# Revit family: IS_Idealrain_Multiproduct_BIM_DE_B9833;B9834;B9835;B9836
name_source: partatom
category: Plumbing Fixtures
revit_build: Autodesk Revit MEP 2016 (Build: 20161004_0715(x64)
units: mm (PartAtom-declared; Revit-internal decimal feet)

## family parameters
Cut with Voids When Loaded = No
Host = Face
OmniClass Number = 23.45.05.14.17
OmniClass Title = Showers
Part Type = Normal
Room Calculation Point = No
Round Connector Dimension = Use Diameter
Shared = Yes

## types (3) — shared parameters
Accessories = www.idealspec.co.uk
AreaUnits = millimeters
Assembly Code = C1030200
AssetType = Fixed
Category = SanitaryTerminal_SHOWER_UK
Color = Chrome
ConnectionType = Plumbing
CurrencyUnit = €
CurrentRevision = 1
Default Elevation = 1750 mm
DrainSize = 0
DurationUnit = year
ExpectedLife = 25
Finish = Chrome
FlowRate = 8 L/min @ 3 bar
InstallationDate = 1900-12-31T23:59:59
InstallationInstructions = www.idealstandard.de\produkte
LinearUnits = millimeters
ManufacturerURL = www.idealstandard.de
Material = Varies
NBSReference = 375
NominalLength = 50 mm  [stored 0.164042 ft]
NominalWidth = 117 mm
ProductDataSheet = www.idealstandard.de\produkte
ProductInformation = www.idealstandard.de
SalesInformation = http://www.idealspec.co.uk
SendEnquiry = http://www.idealspec.co.uk
Shape = Sculptured
ShowerHeadDescription = Handset
ShowerType = Exposed
Space = Internal
SpareParts = www.idealstandard.de/ersatzteile
TMV2 = No
URL = www.idealstandard.de
Uniclass2015Code = Pr_40_20_87_81
Uniclass2015Title = Shower thermostatic water supply sets
Uniclass2015Version = Products v1.1
Version = 1
VolumeUnits = Litres
zero-valued in all types: Cost

## per-type parameters (varying)
| type | BIMObjectName | BarCode | CodePerformance | Description | Features | GrossWeight | Model | ModelNumber | ModelReference | Name | NettWeight | NominalHeight | PartNumber | Size |
| B9833AA - Idealrain Pro M1 Shower Kit With Single Function ø100mm Handspray, 600mm Rail & 1750mm Hose | ISI_IdealStandard_Showers_IDEALRAIN PRO_B9833AA | 3800861030096 |  | Idealrain Pro M1 Shower Kit With Single Function ø100mm Handspray, 600mm Rail & 1750mm Hose | IDEALRAIN PRO shower kit with single function 100mm handspray, 600mm slide rail | 1,542 kg | B9833AA | B9833AA | B9833AA | ISI_IdealStandard_Showers_IDEALRAIN PRO_B9833AA | 1,262 kg | 550 mm | B9833AA | 550 x 150 x 115 mm |
| B9835AA - Idealrain Pro M1 Shower Kit With Single Function ø100mm Handspray, 900mm Rail & 1750mm Hose | ISI_IdealStandard_Showers_IDEALRAIN PRO_B9835AA | 3800861030119 |  | Idealrain Pro M1 Shower Kit With Single Function ø100mm Handspray, 900mm Rail & 1750mm Hose | IDEALRAIN PRO shower kit with single function 100mm handspray, 900mm slide rail | 1,823 kg | B9835AA | B9835AA | B9835AA | ISI_IdealStandard_Showers_IDEALRAIN PRO_B9835AA | 1,412 kg | 850 mm  [stored 2.78871 ft] | B9835AA | 850 x 150 x 115 mm |
| B9836AA - Idealrain Pro M3 Shower Kit With 3 Function ø100mm Handspray, 900mm Rail & 1750mm Hose | ISI_IdealStandard_Showers_IDEALRAIN PRO_B9836AA | 3800861030126 | 0 | Idealrain Pro M3 Shower Kit With 3 Function ø100mm Handspray, 900mm Rail & 1750mm Hose | IDEALRAIN PRO shower kit with 3 function 100mm handspray, 900mm slide rail | 1,871 kg | B9836AA | B9836AA | B9836AA | ISI_IdealStandard_Showers_IDEALRAIN PRO_B9836AA | 1,46 kg | 850 mm  [stored 2.78871 ft] | B9836AA | 850 x 150 x 115 mm |

note: [stored X ft] marks values corroborated as IEEE doubles in the binary element streams (Revit-internal decimal feet)

## geometry (parser evidence)
native form markers: Blend x8, Sweep x2
no freeform markers — native parametric forms only
